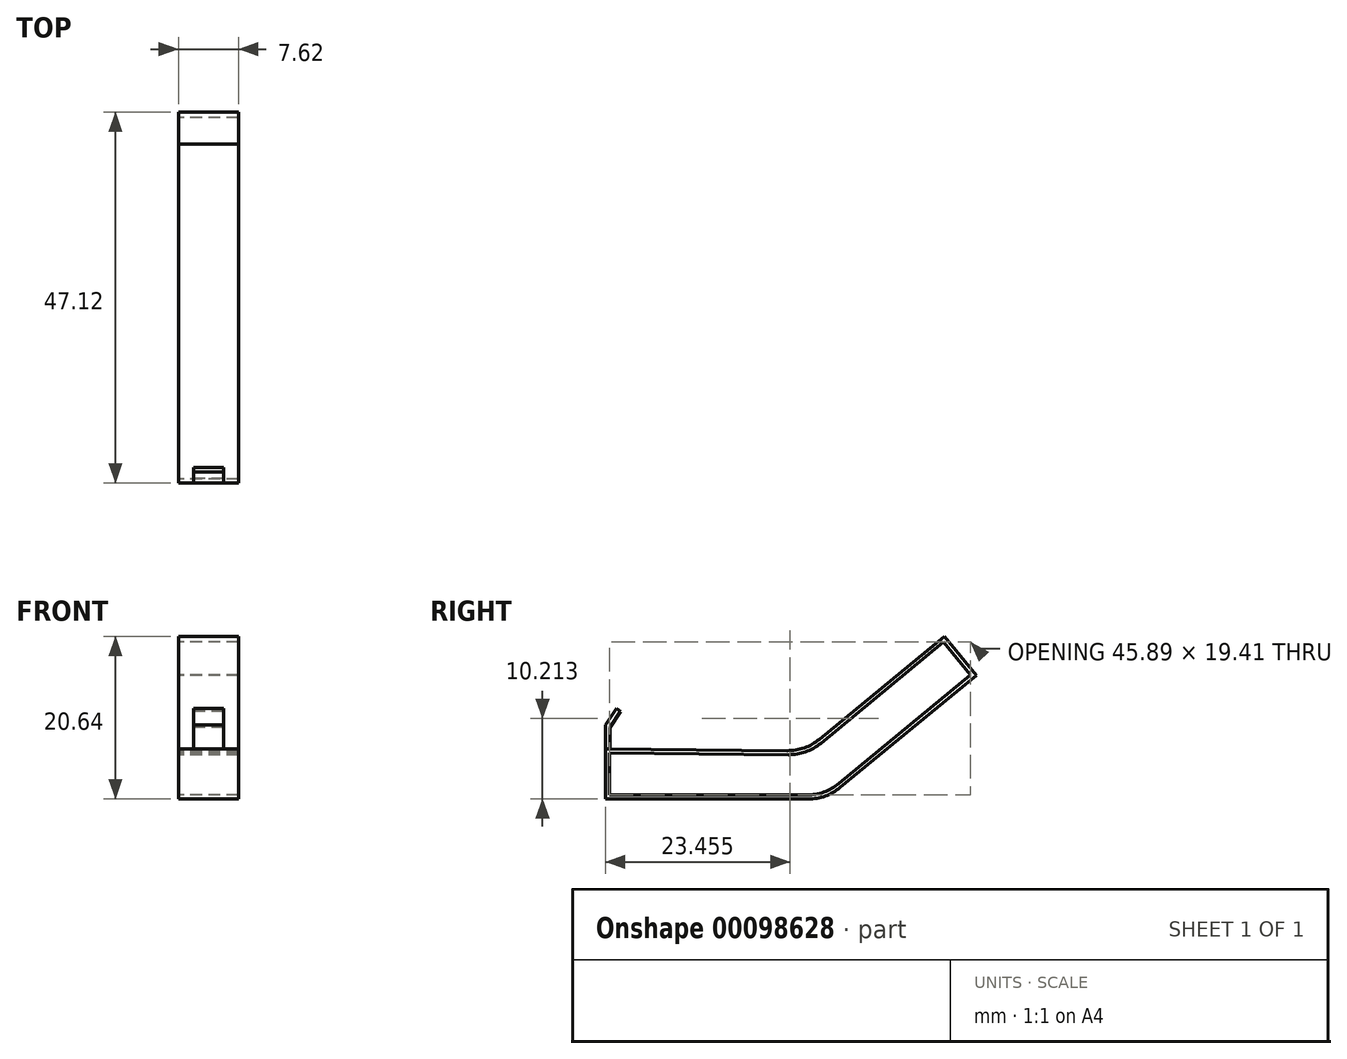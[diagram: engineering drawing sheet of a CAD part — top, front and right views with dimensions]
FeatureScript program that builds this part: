
annotation { "Feature Type Name" : "Feature", "Feature Type Description" : "" }
export const myFeature = defineFeature(function(context is Context, id is Id, definition is map)
    precondition{}
    {
        {
            var Q0;
            Q0=qCreatedBy(makeId("Right.planeOp"),FACE);
            var sketch = newSketch(context, id + "F0", { "sketchPlane" : qUnion([Q0])});
            skLineSegment(sketch, "E0", {"start": v(0, 0) * mm, "end": v(0, 6.35) * mm});
            skLineSegment(sketch, "E1", {"start": v(0, 6.35) * mm, "end": v(23.09, 6.13) * mm});
            skLineSegment(sketch, "E2", {"start": v(27.18, 7.58) * mm, "end": v(43.05, 20.64) * mm});
            skLineSegment(sketch, "E3", {"start": v(0, 0) * mm, "end": v(25.79, 0) * mm});
            skLineSegment(sketch, "E4", {"start": v(29.83, 1.45) * mm, "end": v(47.12, 15.69) * mm});
            skLineSegment(sketch, "E5", {"start": v(43.05, 20.64) * mm, "end": v(47.12, 15.69) * mm});
            skLineSegment(sketch, "E6.0", {"start": v(0, 5.84) * mm, "end": v(0, 5.84) * mm});
            skLineSegment(sketch, "E7.0", {"start": v(0.5, 0.5) * mm, "end": v(0.5, 5.84) * mm});
            skLineSegment(sketch, "E8.0", {"start": v(0.5, 0.5) * mm, "end": v(25.6, 0.5) * mm});
            skLineSegment(sketch, "E9.0", {"start": v(29.64, 1.96) * mm, "end": v(46.4, 15.75) * mm});
            skLineSegment(sketch, "E10.0", {"start": v(27.36, 7.07) * mm, "end": v(42.97, 19.92) * mm});
            skLineSegment(sketch, "E11.trimOffspring", {"start": v(0.5, 5.84) * mm, "end": v(23.27, 5.62) * mm});
            skLineSegment(sketch, "E12.trimOffspring", {"start": v(0.5, 6.35) * mm, "end": v(0.5, 6.35) * mm});
            skLineSegment(sketch, "E13", {"start": v(42.97, 19.92) * mm, "end": v(46.4, 15.75) * mm});
            skPoint(sketch, "E14.visualSharp", {"position": v(25.58, 5.6) * mm});
            skArc(sketch, "E14.filletArc", {"start": v(23.27, 5.62) * mm, "mid": v(25.44, 5.98) * mm, "end": v(27.36, 7.07) * mm});
            skPoint(sketch, "E15.visualSharp", {"position": v(25.4, 6.11) * mm});
            skArc(sketch, "E15.filletArc", {"start": v(23.09, 6.13) * mm, "mid": v(25.26, 6.5) * mm, "end": v(27.18, 7.58) * mm});
            skPoint(sketch, "E16.visualSharp", {"position": v(27.88, 0.5) * mm});
            skArc(sketch, "E16.filletArc", {"start": v(25.6, 0.5) * mm, "mid": v(27.75, 0.88) * mm, "end": v(29.64, 1.96) * mm});
            skPoint(sketch, "E17.visualSharp", {"position": v(28.07, 0) * mm});
            skArc(sketch, "E17.filletArc", {"start": v(25.79, 0) * mm, "mid": v(27.93, 0.37) * mm, "end": v(29.83, 1.45) * mm});
            skSolve(sketch);
        }
        {
            var Q0;
            Q0 = qSketchRegion(id + "F0", true);
            var Q1;
            {var subQ3=sQuery(id+"F0.wireOp",EDGE,"E2");Q1=makeQuery(id+"F0.imprint","IMPRINT",FACE,{"disambiguationData":[TD([[makeQuery(id+"F0.imprint","IMPRINT",EDGE,{"derivedFrom":subQ3}),-1.0]])]});}
            extrude(context, id + "F1", {"entities" : qUnion([Q0, Q1]), "endBound" : BoundingType.SYMMETRIC, "depth" : 7.62 * mm});
        }
        {
            var Q0;
            Q0=qCreatedBy(makeId("Right.planeOp"),FACE);
            var sketch = newSketch(context, id + "F2", { "sketchPlane" : qUnion([Q0])});
            skLineSegment(sketch, "E18", {"start": v(0, 6.36) * mm, "end": v(0, 9.37) * mm});
            skLineSegment(sketch, "E19", {"start": v(0, 9.37) * mm, "end": v(1.39, 11.5) * mm});
            skLineSegment(sketch, "E20", {"start": v(1.39, 11.5) * mm, "end": v(1.94, 11.14) * mm});
            skLineSegment(sketch, "E21", {"start": v(1.94, 11.14) * mm, "end": v(0.6, 9.08) * mm});
            skLineSegment(sketch, "E22", {"start": v(0.6, 6.35) * mm, "end": v(0.6, 9.08) * mm});
            skLineSegment(sketch, "E23", {"start": v(0, 6.36) * mm, "end": v(0.6, 6.35) * mm});
            skSolve(sketch);
        }
        {
            var Q0;
            Q0 = qSketchRegion(id + "F2", true);
            extrude(context, id + "F3", {"entities" : qUnion([Q0]), "endBound" : BoundingType.SYMMETRIC, "depth" : 3.8 * mm});
        }
    });
